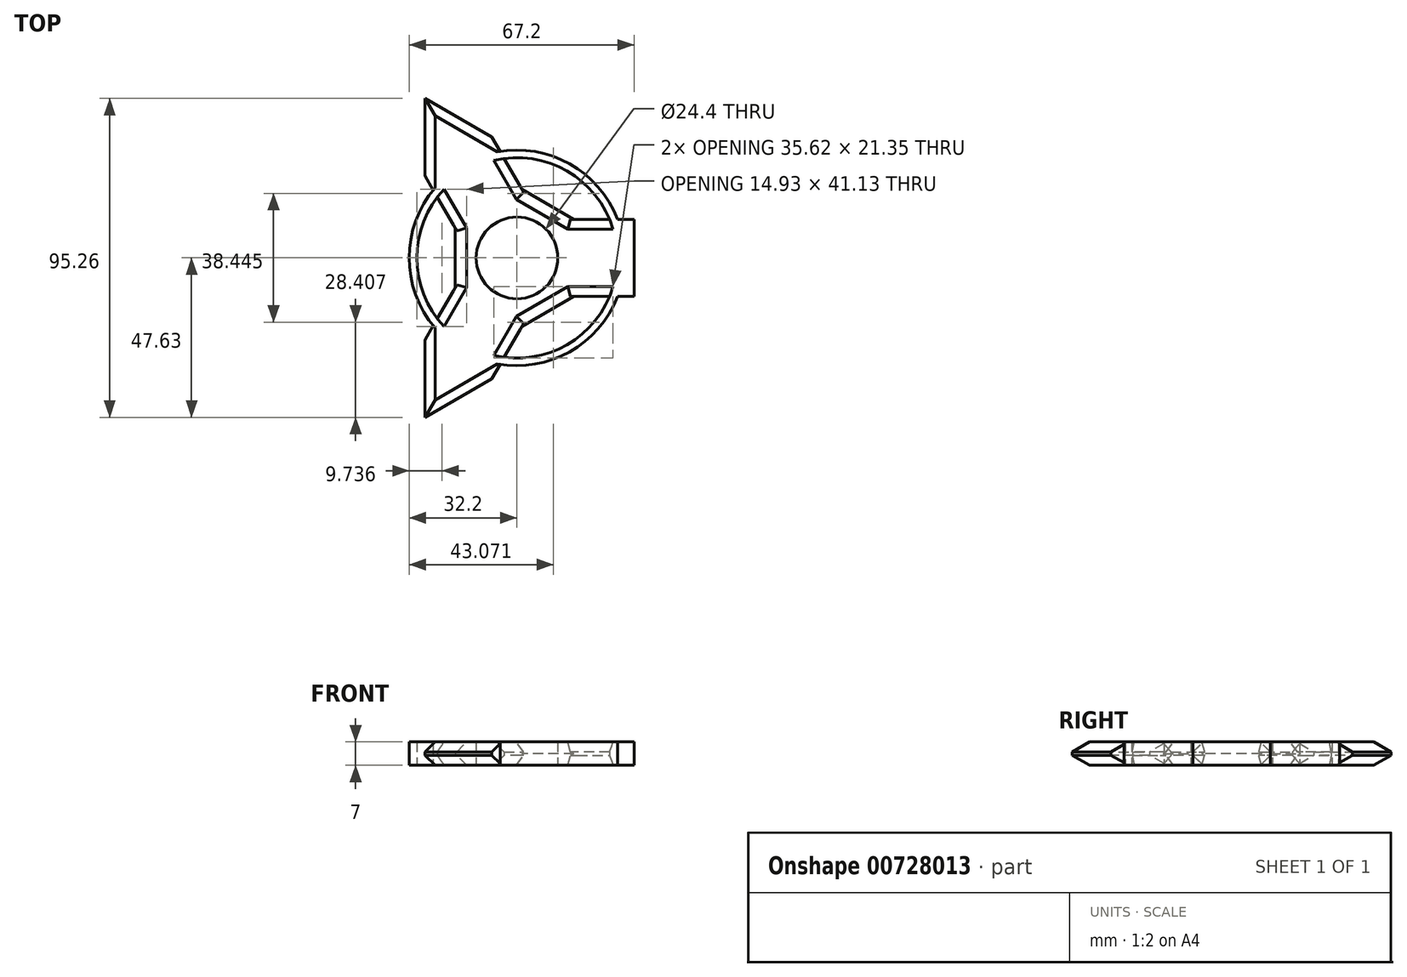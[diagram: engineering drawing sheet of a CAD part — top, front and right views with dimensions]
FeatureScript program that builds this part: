
annotation { "Feature Type Name" : "Feature", "Feature Type Description" : "" }
export const myFeature = defineFeature(function(context is Context, id is Id, definition is map)
    precondition{}
    {
        {
            var Q0;
            Q0=qCreatedBy(makeId("Top.planeOp"),FACE);
            var sketch = newSketch(context, id + "F0", { "sketchPlane" : qUnion([Q0])});
            skCircle(sketch, "E0", {"center": v(0, 0) * mm, "radius": 12.2 * mm});
            skLineSegment(sketch, "E1", {"start": v(0, 0) * mm, "end": v(-20, 0) * mm});
            skLineSegment(sketch, "E2", {"start": v(-20, 0) * mm, "end": v(0, 0) * mm});
            skCircle(sketch, "E3.cCircle", {"center": v(0, 0) * mm, "radius": 20 * mm, "construction": true});
            skLineSegment(sketch, "E3.0", {"start": v(-20, -11.55) * mm, "end": v(-20, 11.55) * mm});
            skLineSegment(sketch, "E3.1", {"start": v(-20, 11.55) * mm, "end": v(0, 23.1) * mm});
            skLineSegment(sketch, "E3.2", {"start": v(0, 23.1) * mm, "end": v(20, 11.55) * mm});
            skLineSegment(sketch, "E3.3", {"start": v(20, 11.55) * mm, "end": v(20, -11.55) * mm});
            skLineSegment(sketch, "E3.4", {"start": v(20, -11.55) * mm, "end": v(0, -23.1) * mm});
            skLineSegment(sketch, "E3.5", {"start": v(0, -23.1) * mm, "end": v(-20, -11.55) * mm});
            skPoint(sketch, "E3.0.midPoint", {"position": v(-20, 0) * mm});
            skLineSegment(sketch, "E4", {"start": v(-20, 11.55) * mm, "end": v(-23.8, 18.14) * mm});
            skLineSegment(sketch, "E5", {"start": v(-27.5, 24.54) * mm, "end": v(0, 23.1) * mm});
            skLineSegment(sketch, "E6", {"start": v(0, 23.1) * mm, "end": v(-3.8, 29.69) * mm});
            skLineSegment(sketch, "E7", {"start": v(-7.5, 36.08) * mm, "end": v(-27.5, 24.54) * mm});
            skLineSegment(sketch, "E8", {"start": v(20, 11.55) * mm, "end": v(27.61, 11.55) * mm});
            skLineSegment(sketch, "E9", {"start": v(35, 11.55) * mm, "end": v(20, -11.55) * mm});
            skLineSegment(sketch, "E10", {"start": v(20, -11.55) * mm, "end": v(27.61, -11.55) * mm});
            skLineSegment(sketch, "E11", {"start": v(35, -11.55) * mm, "end": v(35, 11.55) * mm});
            skLineSegment(sketch, "E12", {"start": v(0, -23.1) * mm, "end": v(-3.8, -29.69) * mm});
            skLineSegment(sketch, "E13", {"start": v(-7.5, -36.08) * mm, "end": v(-20, -11.55) * mm});
            skLineSegment(sketch, "E14", {"start": v(-20, -11.55) * mm, "end": v(-23.8, -18.14) * mm});
            skLineSegment(sketch, "E15", {"start": v(-27.5, -24.54) * mm, "end": v(-7.5, -36.08) * mm});
            skLineSegment(sketch, "E16", {"start": v(35, 11.55) * mm, "end": v(35, -11.55) * mm});
            skLineSegment(sketch, "E17", {"start": v(-27.5, 24.54) * mm, "end": v(-17.5, 30.31) * mm});
            skLineSegment(sketch, "E18", {"start": v(-17.5, 30.31) * mm, "end": v(-27.5, 47.63) * mm});
            skLineSegment(sketch, "E19", {"start": v(-27.5, 47.63) * mm, "end": v(-27.5, 24.54) * mm});
            skLineSegment(sketch, "E20", {"start": v(-27.5, 47.63) * mm, "end": v(-7.5, 36.08) * mm});
            skLineSegment(sketch, "E21", {"start": v(35, 11.55) * mm, "end": v(35, 0) * mm});
            skLineSegment(sketch, "E22", {"start": v(35, 0) * mm, "end": v(55, 0) * mm});
            skLineSegment(sketch, "E23", {"start": v(55, 0) * mm, "end": v(35, 11.55) * mm});
            skLineSegment(sketch, "E24", {"start": v(35, -11.55) * mm, "end": v(55, 0) * mm});
            skLineSegment(sketch, "E25", {"start": v(-17.5, -30.31) * mm, "end": v(-27.5, -47.63) * mm});
            skLineSegment(sketch, "E26", {"start": v(-27.5, -47.63) * mm, "end": v(-27.5, -24.54) * mm});
            skLineSegment(sketch, "E27", {"start": v(-27.5, -47.63) * mm, "end": v(-7.5, -36.08) * mm});
            skArc(sketch, "E28", {"start": v(-25.03, 20.26) * mm, "mid": v(-32.2, 0) * mm, "end": v(-25.03, -20.26) * mm});
            skArc(sketch, "E29", {"start": v(-23.8, 18.14) * mm, "mid": v(-29.93, 0) * mm, "end": v(-23.8, -18.14) * mm});
            skLineSegment(sketch, "E30.trimOffspring", {"start": v(-5.03, 31.8) * mm, "end": v(-7.5, 36.08) * mm});
            skLineSegment(sketch, "E31.trimOffspring", {"start": v(-25.03, 20.26) * mm, "end": v(-27.5, 24.54) * mm});
            skLineSegment(sketch, "E32.trimOffspring", {"start": v(-25.03, -20.26) * mm, "end": v(-27.5, -24.54) * mm});
            skArc(sketch, "E33.trimOffspring", {"start": v(-3.8, -29.69) * mm, "mid": v(14.96, -25.92) * mm, "end": v(27.61, -11.55) * mm});
            skArc(sketch, "E34.trimOffspring", {"start": v(-5.03, -31.8) * mm, "mid": v(16.1, -27.89) * mm, "end": v(30.06, -11.55) * mm});
            skLineSegment(sketch, "E35.trimOffspring", {"start": v(30.06, -11.55) * mm, "end": v(35, -11.55) * mm});
            skLineSegment(sketch, "E36.trimOffspring", {"start": v(-5.03, -31.8) * mm, "end": v(-7.5, -36.08) * mm});
            skLineSegment(sketch, "E37.trimOffspring", {"start": v(30.06, 11.55) * mm, "end": v(35, 11.55) * mm});
            skArc(sketch, "E38.trimOffspring", {"start": v(30.06, 11.55) * mm, "mid": v(16.1, 27.89) * mm, "end": v(-5.03, 31.8) * mm});
            skArc(sketch, "E39.trimOffspring", {"start": v(27.61, 11.55) * mm, "mid": v(14.96, 25.92) * mm, "end": v(-3.8, 29.69) * mm});
            skSolve(sketch);
        }
        {
            var Q0;
            Q0=makeQuery(id+"F0.imprint","IMPRINT",FACE,{"disambiguationData":[TD([[makeQuery(id+"F0.imprint","IMPRINT",EDGE,{"derivedFrom":sQuery(id+"F0.wireOp",EDGE,"E17")}),1.0]])]});
            var Q1;
            Q1=makeQuery(id+"F0.imprint","IMPRINT",FACE,{"disambiguationData":[TD([[makeQuery(id+"F0.imprint","IMPRINT",EDGE,{"derivedFrom":sQuery(id+"F0.wireOp",EDGE,"E7")}),-1.0]])]});
            var Q2;
            Q2=makeQuery(id+"F0.imprint","IMPRINT",FACE,{"disambiguationData":[TD([[makeQuery(id+"F0.imprint","IMPRINT",EDGE,{"derivedFrom":sQuery(id+"F0.wireOp",EDGE,"E5")}),1.0]])]});
            var Q3;
            Q3=makeQuery(id+"F0.imprint","IMPRINT",FACE,{"disambiguationData":[TD([[makeQuery(id+"F0.imprint","IMPRINT",EDGE,{"derivedFrom":sQuery(id+"F0.wireOp",EDGE,"E3.1")}),1.0]])]});
            var Q4;
            Q4=makeQuery(id+"F0.imprint","IMPRINT",FACE,{"disambiguationData":[TD([[makeQuery(id+"F0.imprint","IMPRINT",EDGE,{"derivedFrom":sQuery(id+"F0.wireOp",EDGE,"E0")}),-1.0]])]});
            var Q5;
            Q5=makeQuery(id+"F0.imprint","IMPRINT",FACE,{"disambiguationData":[TD([[makeQuery(id+"F0.imprint","IMPRINT",EDGE,{"derivedFrom":sQuery(id+"F0.wireOp",EDGE,"E3.3")}),1.0]])]});
            var Q6;
            Q6=makeQuery(id+"F0.imprint","IMPRINT",FACE,{"disambiguationData":[TD([[makeQuery(id+"F0.imprint","IMPRINT",EDGE,{"derivedFrom":sQuery(id+"F0.wireOp",EDGE,"E9")}),1.0]])]});
            var Q7;
            Q7=makeQuery(id+"F0.imprint","IMPRINT",FACE,{"disambiguationData":[TD([[makeQuery(id+"F0.imprint","IMPRINT",EDGE,{"derivedFrom":sQuery(id+"F0.wireOp",EDGE,"E21")}),1.0]])]});
            var Q8;
            Q8=makeQuery(id+"F0.imprint","IMPRINT",FACE,{"disambiguationData":[TD([[makeQuery(id+"F0.imprint","IMPRINT",EDGE,{"derivedFrom":sQuery(id+"F0.wireOp",EDGE,"E16")}),1.0]])]});
            var Q9;
            Q9=makeQuery(id+"F0.imprint","IMPRINT",FACE,{"disambiguationData":[TD([[makeQuery(id+"F0.imprint","IMPRINT",EDGE,{"derivedFrom":sQuery(id+"F0.wireOp",EDGE,"E3.5")}),1.0]])]});
            var Q10;
            {var subQ2=sQuery(id+"F0.wireOp",EDGE,"E25");Q10=makeQuery(id+"F0.imprint","IMPRINT",FACE,{"disambiguationData":[TD([[makeQuery(id+"F0.imprint","IMPRINT",EDGE,{"derivedFrom":subQ2}),1.0]])]});}
            var Q11;
            {var subQ2=sQuery(id+"F0.wireOp",EDGE,"E25");Q11=makeQuery(id+"F0.imprint","IMPRINT",FACE,{"disambiguationData":[TD([[makeQuery(id+"F0.imprint","IMPRINT",EDGE,{"derivedFrom":subQ2}),-1.0]])]});}
            var Q12;
            {var subQ0=sQuery(id+"F0.wireOp",EDGE,"E13");Q12=makeQuery(id+"F0.imprint","IMPRINT",FACE,{"disambiguationData":[TD([[makeQuery(id+"F0.imprint","IMPRINT",EDGE,{"derivedFrom":subQ0}),1.0]])]});}
            extrude(context, id + "F1", {"entities" : qUnion([Q0, Q1, Q2, Q3, Q4, Q5, Q6, Q7, Q8, Q9, Q10, Q11, Q12]), "depth" : 7 * mm, "offsetDistance" : 25 * mm});
        }
        {
            var Q0;
            Q0=makeQuery(id+"F1.opExtrude","CAP_EDGE",EDGE,{"disambiguationData":[OSD([sQuery(id+"F0.wireOp",EDGE,"E19")])],"isStart":false});
            var Q1;
            Q1=makeQuery(id+"F1.opExtrude","CAP_EDGE",EDGE,{"disambiguationData":[OSD([sQuery(id+"F0.wireOp",EDGE,"E6")])],"isStart":false});
            var Q2;
            Q2=makeQuery(id+"F1.opExtrude","CAP_EDGE",EDGE,{"disambiguationData":[OSD([sQuery(id+"F0.wireOp",EDGE,"E4")])],"isStart":false});
            var Q3;
            Q3=makeQuery(id+"F1.opExtrude","CAP_EDGE",EDGE,{"disambiguationData":[OSD([sQuery(id+"F0.wireOp",EDGE,"E20")])],"isStart":false});
            var Q4;
            Q4=makeQuery(id+"F1.opExtrude","CAP_EDGE",EDGE,{"disambiguationData":[OSD([sQuery(id+"F0.wireOp",EDGE,"E8")])],"isStart":false});
            var Q5;
            Q5=makeQuery(id+"F1.opExtrude","CAP_EDGE",EDGE,{"disambiguationData":[OSD([sQuery(id+"F0.wireOp",EDGE,"E23")])],"isStart":false});
            var Q6;
            Q6=makeQuery(id+"F1.opExtrude","CAP_EDGE",EDGE,{"disambiguationData":[OSD([sQuery(id+"F0.wireOp",EDGE,"E24")])],"isStart":false});
            var Q7;
            Q7=makeQuery(id+"F1.opExtrude","CAP_EDGE",EDGE,{"disambiguationData":[OSD([sQuery(id+"F0.wireOp",EDGE,"E10")])],"isStart":false});
            var Q8;
            Q8=makeQuery(id+"F1.opExtrude","CAP_EDGE",EDGE,{"disambiguationData":[OSD([sQuery(id+"F0.wireOp",EDGE,"E12")])],"isStart":false});
            var Q9;
            Q9=makeQuery(id+"F1.opExtrude","CAP_EDGE",EDGE,{"disambiguationData":[OSD([sQuery(id+"F0.wireOp",EDGE,"E27")])],"isStart":false});
            var Q10;
            Q10=makeQuery(id+"F1.opExtrude","CAP_EDGE",EDGE,{"disambiguationData":[OSD([sQuery(id+"F0.wireOp",EDGE,"E26")])],"isStart":false});
            var Q11;
            Q11=makeQuery(id+"F1.opExtrude","CAP_EDGE",EDGE,{"disambiguationData":[OSD([sQuery(id+"F0.wireOp",EDGE,"E14")])],"isStart":false});
            var Q12;
            Q12=makeQuery(id+"F1.opExtrude","CAP_EDGE",EDGE,{"disambiguationData":[OSD([sQuery(id+"F0.wireOp",EDGE,"E20")])],"isStart":true});
            var Q13;
            Q13=makeQuery(id+"F1.opExtrude","CAP_EDGE",EDGE,{"disambiguationData":[OSD([sQuery(id+"F0.wireOp",EDGE,"E19")])],"isStart":true});
            var Q14;
            Q14=makeQuery(id+"F1.opExtrude","CAP_EDGE",EDGE,{"disambiguationData":[OSD([sQuery(id+"F0.wireOp",EDGE,"E6")])],"isStart":true});
            var Q15;
            Q15=makeQuery(id+"F1.opExtrude","CAP_EDGE",EDGE,{"disambiguationData":[OSD([sQuery(id+"F0.wireOp",EDGE,"E4")])],"isStart":true});
            var Q16;
            Q16=makeQuery(id+"F1.opExtrude","CAP_EDGE",EDGE,{"disambiguationData":[OSD([sQuery(id+"F0.wireOp",EDGE,"E14")])],"isStart":true});
            var Q17;
            Q17=makeQuery(id+"F1.opExtrude","CAP_EDGE",EDGE,{"disambiguationData":[OSD([sQuery(id+"F0.wireOp",EDGE,"E26")])],"isStart":true});
            var Q18;
            Q18=makeQuery(id+"F1.opExtrude","CAP_EDGE",EDGE,{"disambiguationData":[OSD([sQuery(id+"F0.wireOp",EDGE,"E27")])],"isStart":true});
            var Q19;
            Q19=makeQuery(id+"F1.opExtrude","CAP_EDGE",EDGE,{"disambiguationData":[OSD([sQuery(id+"F0.wireOp",EDGE,"E12")])],"isStart":true});
            var Q20;
            Q20=makeQuery(id+"F1.opExtrude","CAP_EDGE",EDGE,{"disambiguationData":[OSD([sQuery(id+"F0.wireOp",EDGE,"E10")])],"isStart":true});
            var Q21;
            Q21=makeQuery(id+"F1.opExtrude","CAP_EDGE",EDGE,{"disambiguationData":[OSD([sQuery(id+"F0.wireOp",EDGE,"E24")])],"isStart":true});
            var Q22;
            Q22=makeQuery(id+"F1.opExtrude","CAP_EDGE",EDGE,{"disambiguationData":[OSD([sQuery(id+"F0.wireOp",EDGE,"E23")])],"isStart":true});
            var Q23;
            Q23=makeQuery(id+"F1.opExtrude","CAP_EDGE",EDGE,{"disambiguationData":[OSD([sQuery(id+"F0.wireOp",EDGE,"E8")])],"isStart":true});
            chamfer(context, id + "F2", {"entities" : qUnion([Q0, Q1, Q2, Q3, Q4, Q5, Q6, Q7, Q8, Q9, Q10, Q11, Q12, Q13, Q14, Q15, Q16, Q17, Q18, Q19, Q20, Q21, Q22, Q23]), "width" : 3 * mm, "tangentPropagation" : true});
        }
        {
            var Q0;
            Q0=makeQuery(id+"F1.opExtrude","CAP_EDGE",EDGE,{"disambiguationData":[OSD([sQuery(id+"F0.wireOp",EDGE,"E3.2")])],"isStart":true});
            var Q1;
            Q1=makeQuery(id+"F1.opExtrude","CAP_EDGE",EDGE,{"disambiguationData":[OSD([sQuery(id+"F0.wireOp",EDGE,"E3.0")])],"isStart":true});
            var Q2;
            Q2=makeQuery(id+"F1.opExtrude","CAP_EDGE",EDGE,{"disambiguationData":[OSD([sQuery(id+"F0.wireOp",EDGE,"E3.4")])],"isStart":true});
            var Q3;
            Q3=makeQuery(id+"F1.opExtrude","CAP_EDGE",EDGE,{"disambiguationData":[OSD([sQuery(id+"F0.wireOp",EDGE,"E3.0")])],"isStart":false});
            var Q4;
            Q4=makeQuery(id+"F1.opExtrude","CAP_EDGE",EDGE,{"disambiguationData":[OSD([sQuery(id+"F0.wireOp",EDGE,"E3.2")])],"isStart":false});
            var Q5;
            Q5=makeQuery(id+"F1.opExtrude","CAP_EDGE",EDGE,{"disambiguationData":[OSD([sQuery(id+"F0.wireOp",EDGE,"E3.4")])],"isStart":false});
            chamfer(context, id + "F3", {"entities" : qUnion([Q0, Q1, Q2, Q3, Q4, Q5]), "width" : 5 * mm, "tangentPropagation" : true});
        }
    });
